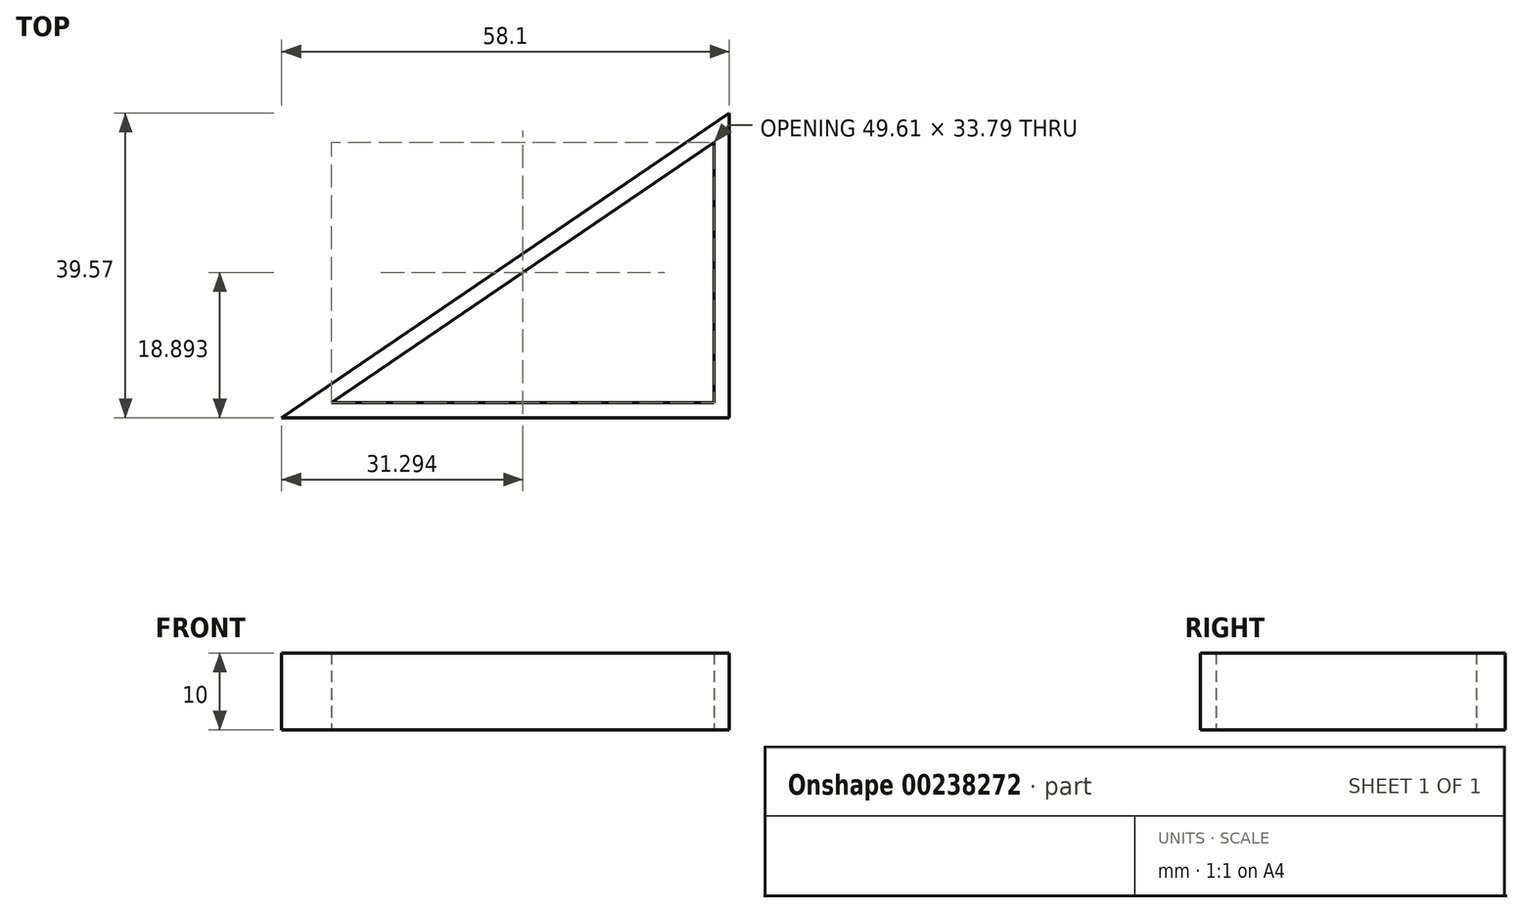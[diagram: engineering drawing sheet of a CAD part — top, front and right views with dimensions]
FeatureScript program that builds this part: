
annotation { "Feature Type Name" : "Feature", "Feature Type Description" : "" }
export const myFeature = defineFeature(function(context is Context, id is Id, definition is map)
    precondition{}
    {
        {
            var Q0;
            Q0=qCreatedBy(makeId("Top.planeOp"),FACE);
            var sketch = newSketch(context, id + "F0", { "sketchPlane" : qUnion([Q0])});
            skLineSegment(sketch, "E0", {"start": v(0, 0) * mm, "end": v(-58.1, 0) * mm});
            skLineSegment(sketch, "E1", {"start": v(0, 0) * mm, "end": v(0, 39.57) * mm});
            skLineSegment(sketch, "E2", {"start": v(0, 39.57) * mm, "end": v(-58.1, 0) * mm});
            skLineSegment(sketch, "E3.0", {"start": v(-2, 35.79) * mm, "end": v(-51.61, 2) * mm});
            skLineSegment(sketch, "E3.1", {"start": v(-2, 2) * mm, "end": v(-2, 35.79) * mm});
            skLineSegment(sketch, "E3.2", {"start": v(-2, 2) * mm, "end": v(-51.61, 2) * mm});
            skSolve(sketch);
        }
        {
            var Q0;
            Q0=makeQuery(id+"F0.imprint","IMPRINT",FACE,{"disambiguationData":[TD([[makeQuery(id+"F0.imprint","IMPRINT",EDGE,{"derivedFrom":sQuery(id+"F0.wireOp",EDGE,"E0")}),-1.0]])]});
            extrude(context, id + "F1", {"entities" : qUnion([Q0]), "depth" : 10 * mm});
        }
    });
